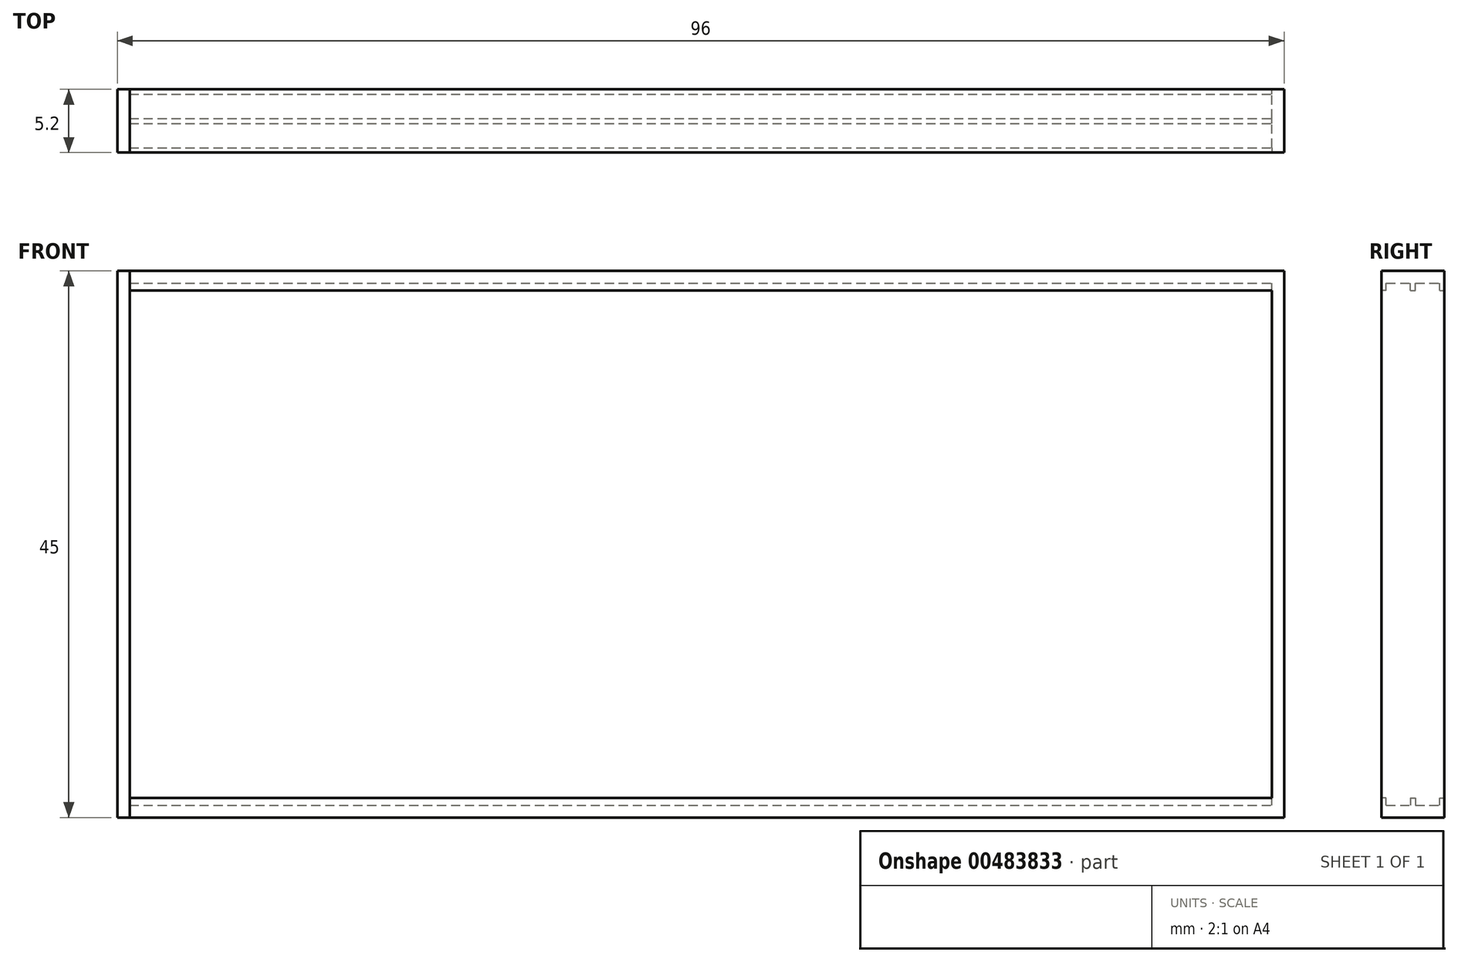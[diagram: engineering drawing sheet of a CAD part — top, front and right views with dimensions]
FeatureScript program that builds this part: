
annotation { "Feature Type Name" : "Feature", "Feature Type Description" : "" }
export const myFeature = defineFeature(function(context is Context, id is Id, definition is map)
    precondition{}
    {
        {
            var Q0;
            Q0=qCreatedBy(makeId("Front.planeOp"),FACE);
            var sketch = newSketch(context, id + "F0", { "sketchPlane" : qUnion([Q0])});
            skLineSegment(sketch, "E0.bottom", {"start": v(1, 0) * mm, "end": v(96, 0) * mm});
            skLineSegment(sketch, "E0.top", {"start": v(1, 45) * mm, "end": v(96, 45) * mm});
            skLineSegment(sketch, "E0.right", {"start": v(96, 0) * mm, "end": v(96, 45) * mm});
            skLineSegment(sketch, "E1.0", {"start": v(1, 44) * mm, "end": v(95, 44) * mm});
            skLineSegment(sketch, "E2.0", {"start": v(1, 1) * mm, "end": v(95, 1) * mm});
            skLineSegment(sketch, "E3.0", {"start": v(95, 1) * mm, "end": v(95, 44) * mm});
            skLineSegment(sketch, "E4", {"start": v(1, 44) * mm, "end": v(1, 45) * mm});
            skLineSegment(sketch, "E5", {"start": v(1, 1) * mm, "end": v(1, 0) * mm});
            skSolve(sketch);
        }
        {
            var Q0;
            Q0 = qSketchRegion(id + "F0", true);
            extrude(context, id + "F1", {"entities" : qUnion([Q0]), "endBound" : BoundingType.SYMMETRIC, "depth" : 5.2 * mm});
        }
        {
            var Q0;
            Q0=qCreatedBy(makeId("Front.planeOp"),FACE);
            var sketch = newSketch(context, id + "F2", { "sketchPlane" : qUnion([Q0])});
            skLineSegment(sketch, "E6.bottom", {"start": v(1, 44) * mm, "end": v(95, 44) * mm});
            skLineSegment(sketch, "E6.top", {"start": v(1, 1) * mm, "end": v(95, 1) * mm});
            skLineSegment(sketch, "E7.0", {"start": v(1, 1.6) * mm, "end": v(95, 1.6) * mm});
            skLineSegment(sketch, "E8.0", {"start": v(1, 43.4) * mm, "end": v(95, 43.4) * mm});
            skLineSegment(sketch, "E9", {"start": v(1, 43.4) * mm, "end": v(1, 44) * mm});
            skLineSegment(sketch, "E10", {"start": v(95, 43.4) * mm, "end": v(95, 44) * mm});
            skLineSegment(sketch, "E11", {"start": v(95, 1.6) * mm, "end": v(95, 1) * mm});
            skLineSegment(sketch, "E12", {"start": v(1, 1.6) * mm, "end": v(1, 1) * mm});
            skSolve(sketch);
        }
        {
            var Q0;
            Q0 = qSketchRegion(id + "F2", true);
            extrude(context, id + "F3", {"entities" : qUnion([Q0]), "operationType" : NewBodyOperationType.ADD, "endBound" : BoundingType.SYMMETRIC, "depth" : 0.4 * mm});
        }
        {
            var Q0;
            Q0=makeQuery(id+"F1.opExtrude","CAP_FACE",FACE,{"disambiguationData":[OSD([sQuery(id+"F0.wireOp",EDGE,"E0.bottom"),sQuery(id+"F0.wireOp",EDGE,"E0.top"),sQuery(id+"F0.wireOp",EDGE,"E0.left"),sQuery(id+"F0.wireOp",EDGE,"E0.right"),sQuery(id+"F0.wireOp",EDGE,"E1.0"),sQuery(id+"F0.wireOp",EDGE,"5e28b8c3-1b48-48a0-a48e-2c2adaf0de72.0"),sQuery(id+"F0.wireOp",EDGE,"E2.0"),sQuery(id+"F0.wireOp",EDGE,"E3.0")])],"isStart":false});
            var sketch = newSketch(context, id + "F4", { "sketchPlane" : qUnion([Q0])});
            skLineSegment(sketch, "E13.bottom", {"start": v(95, 44) * mm, "end": v(95, 44) * mm});
            skLineSegment(sketch, "E13.top", {"start": v(95, 43.4) * mm, "end": v(95, 43.4) * mm});
            skLineSegment(sketch, "E14.bottom", {"start": v(1, 1.6) * mm, "end": v(95, 1.6) * mm});
            skLineSegment(sketch, "E14.top", {"start": v(1, 1) * mm, "end": v(95, 1) * mm});
            skLineSegment(sketch, "E14.left", {"start": v(1, 1.6) * mm, "end": v(1, 1) * mm});
            skLineSegment(sketch, "E14.right", {"start": v(95, 1.6) * mm, "end": v(95, 1) * mm});
            skLineSegment(sketch, "E15.bottom", {"start": v(1, 44) * mm, "end": v(95, 44) * mm});
            skLineSegment(sketch, "E15.top", {"start": v(1, 43.4) * mm, "end": v(95, 43.4) * mm});
            skLineSegment(sketch, "E15.left", {"start": v(1, 44) * mm, "end": v(1, 43.4) * mm});
            skLineSegment(sketch, "E15.right", {"start": v(95, 44) * mm, "end": v(95, 43.4) * mm});
            skSolve(sketch);
        }
        {
            var Q0;
            Q0 = qSketchRegion(id + "F4", true);
            extrude(context, id + "F5", {"entities" : qUnion([Q0]), "operationType" : NewBodyOperationType.ADD, "oppositeDirection" : true, "depth" : 0.4 * mm});
        }
        {
            var Q0;
            Q0=makeQuery(id+"F1.opExtrude","CAP_FACE",FACE,{"disambiguationData":[OSD([sQuery(id+"F0.wireOp",EDGE,"E0.bottom"),sQuery(id+"F0.wireOp",EDGE,"E0.top"),sQuery(id+"F0.wireOp",EDGE,"E0.left"),sQuery(id+"F0.wireOp",EDGE,"E0.right"),sQuery(id+"F0.wireOp",EDGE,"E1.0"),sQuery(id+"F0.wireOp",EDGE,"5e28b8c3-1b48-48a0-a48e-2c2adaf0de72.0"),sQuery(id+"F0.wireOp",EDGE,"E2.0"),sQuery(id+"F0.wireOp",EDGE,"E3.0")])],"isStart":true});
            var sketch = newSketch(context, id + "F6", { "sketchPlane" : qUnion([Q0])});
            skLineSegment(sketch, "E16.bottom", {"start": v(-95, 1.6) * mm, "end": v(-1, 1.6) * mm});
            skLineSegment(sketch, "E16.top", {"start": v(-95, 1) * mm, "end": v(-1, 1) * mm});
            skLineSegment(sketch, "E16.left", {"start": v(-95, 1.6) * mm, "end": v(-95, 1) * mm});
            skLineSegment(sketch, "E16.right", {"start": v(-1, 1.6) * mm, "end": v(-1, 1) * mm});
            skLineSegment(sketch, "E17.bottom", {"start": v(-95, 44) * mm, "end": v(-1, 44) * mm});
            skLineSegment(sketch, "E17.top", {"start": v(-95, 43.4) * mm, "end": v(-1, 43.4) * mm});
            skLineSegment(sketch, "E17.left", {"start": v(-95, 44) * mm, "end": v(-95, 43.4) * mm});
            skLineSegment(sketch, "E17.right", {"start": v(-1, 44) * mm, "end": v(-1, 43.4) * mm});
            skSolve(sketch);
        }
        {
            var Q0;
            Q0 = qSketchRegion(id + "F6", true);
            extrude(context, id + "F7", {"entities" : qUnion([Q0]), "operationType" : NewBodyOperationType.ADD, "oppositeDirection" : true, "depth" : 0.4 * mm});
        }
        {
            var Q0;
            Q0=makeQuery(id+"F7.boolean.opBoolean","MERGE",FACE,{"derivedFrom":[makeQuery(id+"F5.boolean.opBoolean","MERGE",FACE,{"derivedFrom":[makeQuery(id+"F3.boolean.opBoolean","MERGE",FACE,{"derivedFrom":[makeQuery(id+"F1.opExtrude","SWEPT_FACE",FACE,{"disambiguationData":[OSD([sQuery(id+"F0.wireOp",EDGE,"E4")])]}),makeQuery(id+"F3.opExtrude","SWEPT_FACE",FACE,{"disambiguationData":[OSD([sQuery(id+"F2.wireOp",EDGE,"E9")])]})]}),makeQuery(id+"F5.opExtrude","SWEPT_FACE",FACE,{"disambiguationData":[OSD([sQuery(id+"F4.wireOp",EDGE,"E15.left")])]})]}),makeQuery(id+"F7.opExtrude","SWEPT_FACE",FACE,{"disambiguationData":[OSD([sQuery(id+"F6.wireOp",EDGE,"E17.right")])]})]});
            var sketch = newSketch(context, id + "F8", { "sketchPlane" : qUnion([Q0])});
            skLineSegment(sketch, "E18.bottom", {"start": v(-2.6, 45) * mm, "end": v(2.6, 45) * mm});
            skLineSegment(sketch, "E18.top", {"start": v(-2.6, 0) * mm, "end": v(2.6, 0) * mm});
            skLineSegment(sketch, "E18.left", {"start": v(-2.6, 45) * mm, "end": v(-2.6, 0) * mm});
            skLineSegment(sketch, "E18.right", {"start": v(2.6, 45) * mm, "end": v(2.6, 0) * mm});
            skSolve(sketch);
        }
        {
            var Q0;
            Q0 = qSketchRegion(id + "F8", true);
            extrude(context, id + "F9", {"entities" : qUnion([Q0]), "depth" : 1 * mm});
        }
    });
